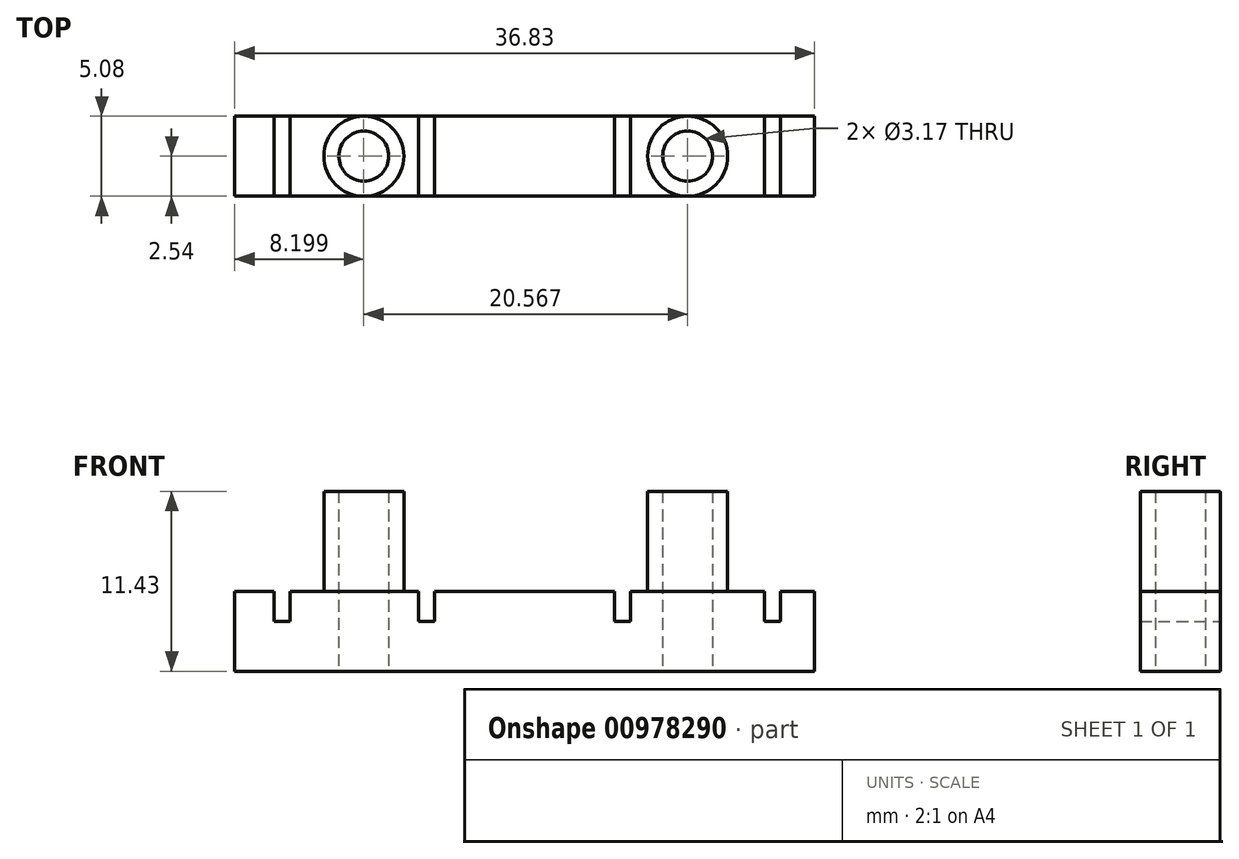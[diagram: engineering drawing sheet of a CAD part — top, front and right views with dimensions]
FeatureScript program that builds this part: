
annotation { "Feature Type Name" : "Feature", "Feature Type Description" : "" }
export const myFeature = defineFeature(function(context is Context, id is Id, definition is map)
    precondition{}
    {
        {
            var Q0;
            Q0=qCreatedBy(makeId("Top.planeOp"),FACE);
            var sketch = newSketch(context, id + "F0", { "sketchPlane" : qUnion([Q0])});
            skLineSegment(sketch, "E0.bottom", {"start": v(-18.67, 0) * mm, "end": v(18.16, 0) * mm});
            skLineSegment(sketch, "E0.top", {"start": v(-18.67, 5.08) * mm, "end": v(18.16, 5.08) * mm});
            skLineSegment(sketch, "E0.left", {"start": v(-18.67, 0) * mm, "end": v(-18.67, 5.08) * mm});
            skLineSegment(sketch, "E0.right", {"start": v(18.16, 0) * mm, "end": v(18.16, 5.08) * mm});
            skSolve(sketch);
        }
        {
            var Q0;
            Q0=makeQuery(id+"F0.imprint","IMPRINT",FACE,{"disambiguationData":[TD([[makeQuery(id+"F0.imprint","IMPRINT",EDGE,{"derivedFrom":sQuery(id+"F0.wireOp",EDGE,"E0.bottom")}),1.0]])]});
            extrude(context, id + "F1", {"entities" : qUnion([Q0]), "depth" : 5.08 * mm, "offsetDistance" : 25.4 * mm});
        }
        {
            var Q0;
            Q0=makeQuery(id+"F1.opExtrude","SWEPT_FACE",FACE,{"disambiguationData":[OSD([sQuery(id+"F0.wireOp",EDGE,"E0.bottom")])]});
            var sketch = newSketch(context, id + "F2", { "sketchPlane" : qUnion([Q0])});
            skCircle(sketch, "E1.cCircle", {"center": v(-15.5, 5.1) * mm, "radius": 0.73 * mm, "construction": true});
            skLineSegment(sketch, "E1.0", {"start": v(-14.22, 5.84) * mm, "end": v(-15.5, 3.64) * mm});
            skLineSegment(sketch, "E1.1", {"start": v(-15.5, 3.64) * mm, "end": v(-16.76, 5.84) * mm});
            skLineSegment(sketch, "E1.2", {"start": v(-16.76, 5.84) * mm, "end": v(-14.22, 5.84) * mm});
            skPoint(sketch, "E1.0.midPoint", {"position": v(-14.86, 4.74) * mm});
            skCircle(sketch, "E2.cCircle", {"center": v(-5.33, 4.85) * mm, "radius": 0.73 * mm, "construction": true});
            skLineSegment(sketch, "E2.0", {"start": v(-4.06, 5.59) * mm, "end": v(-5.33, 3.39) * mm});
            skLineSegment(sketch, "E2.1", {"start": v(-5.33, 3.39) * mm, "end": v(-6.6, 5.59) * mm});
            skLineSegment(sketch, "E2.2", {"start": v(-6.6, 5.59) * mm, "end": v(-4.06, 5.59) * mm});
            skPoint(sketch, "E2.0.midPoint", {"position": v(-4.7, 4.49) * mm});
            skCircle(sketch, "E3.cCircle", {"center": v(14.99, 5.1) * mm, "radius": 0.73 * mm, "construction": true});
            skLineSegment(sketch, "E3.0", {"start": v(16.26, 5.84) * mm, "end": v(14.99, 3.64) * mm});
            skLineSegment(sketch, "E3.1", {"start": v(14.99, 3.64) * mm, "end": v(13.72, 5.84) * mm});
            skLineSegment(sketch, "E3.2", {"start": v(13.72, 5.84) * mm, "end": v(16.26, 5.84) * mm});
            skPoint(sketch, "E3.0.midPoint", {"position": v(15.62, 4.74) * mm});
            skCircle(sketch, "E4.cCircle", {"center": v(4.83, 5.1) * mm, "radius": 0.73 * mm, "construction": true});
            skLineSegment(sketch, "E4.0", {"start": v(6.1, 5.84) * mm, "end": v(4.83, 3.64) * mm});
            skLineSegment(sketch, "E4.1", {"start": v(4.83, 3.64) * mm, "end": v(3.56, 5.84) * mm});
            skLineSegment(sketch, "E4.2", {"start": v(3.56, 5.84) * mm, "end": v(6.1, 5.84) * mm});
            skPoint(sketch, "E4.0.midPoint", {"position": v(5.46, 4.74) * mm});
            skSolve(sketch);
        }
        {
            var Q0;
            {var subQ0=sQuery(id+"F0.wireOp",EDGE,"E0.bottom");var subQ1=sQuery(id+"F0.wireOp",EDGE,"E0.top");Q0=makeQuery(id+"FROfRwlPDn9hxb0_1.boolean.opBoolean","SPLIT",FACE,{"disambiguationData":[TD([makeQuery(id+"FROfRwlPDn9hxb0_1.opExtrude","SWEPT_FACE",FACE,{"disambiguationData":[OSD([sQuery(id+"F2.wireOp",EDGE,"E2.0")])]})])],"derivedFrom":makeQuery(id+"F1.opExtrude","CAP_FACE",FACE,{"disambiguationData":[OSD([subQ0,subQ1,sQuery(id+"F0.wireOp",EDGE,"E0.left"),sQuery(id+"F0.wireOp",EDGE,"E0.right")])],"isStart":false})});}
            var sketch = newSketch(context, id + "F3", { "sketchPlane" : qUnion([Q0])});
            skCircle(sketch, "E5", {"center": v(-0.25, 2.54) * mm, "radius": 2.54 * mm});
            skPoint(sketch, "E5.centerSnap0", {"position": v(-4.43, 2.54) * mm});
            skPoint(sketch, "E5.centerSnap1", {"position": v(-0.25, 0) * mm});
            skCircle(sketch, "E6", {"center": v(-0.25, 2.54) * mm, "radius": 1.59 * mm});
            skCircle(sketch, "E7", {"center": v(-10.47, 2.54) * mm, "radius": 2.54 * mm});
            skCircle(sketch, "E8", {"center": v(-10.47, 2.54) * mm, "radius": 1.59 * mm});
            skCircle(sketch, "E9", {"center": v(10.1, 2.54) * mm, "radius": 2.54 * mm});
            skCircle(sketch, "E10", {"center": v(10.1, 2.54) * mm, "radius": 1.59 * mm});
            skSolve(sketch);
        }
        {
            var Q0;
            Q0=makeQuery(id+"F3.imprint","IMPRINT",FACE,{"disambiguationData":[TD([[makeQuery(id+"F3.imprint","IMPRINT",EDGE,{"derivedFrom":sQuery(id+"F3.wireOp",EDGE,"E7")}),1.0]])]});
            var Q1;
            Q1=makeQuery(id+"F3.imprint","IMPRINT",FACE,{"disambiguationData":[TD([[makeQuery(id+"F3.imprint","IMPRINT",EDGE,{"derivedFrom":sQuery(id+"F3.wireOp",EDGE,"E9")}),1.0]])]});
            extrude(context, id + "F4", {"entities" : qUnion([Q0, Q1]), "operationType" : NewBodyOperationType.ADD, "depth" : 6.35 * mm, "offsetDistance" : 25.4 * mm});
        }
        {
            var Q0;
            {var subQ0=sQuery(id+"F0.wireOp",EDGE,"E0.bottom");var subQ1=sQuery(id+"F0.wireOp",EDGE,"E0.top");Q0=makeQuery(id+"F4.boolean.opBoolean","SPLIT",FACE,{"disambiguationData":[TD([makeQuery(id+"F4.opExtrude","SWEPT_FACE",FACE,{"disambiguationData":[OSD([sQuery(id+"F3.wireOp",EDGE,"E8")])]})])],"derivedFrom":makeQuery(id+"FROfRwlPDn9hxb0_1.boolean.opBoolean","SPLIT",FACE,{"disambiguationData":[TD([makeQuery(id+"FROfRwlPDn9hxb0_1.opExtrude","SWEPT_FACE",FACE,{"disambiguationData":[OSD([sQuery(id+"F2.wireOp",EDGE,"E1.0")])]})])],"derivedFrom":makeQuery(id+"F1.opExtrude","CAP_FACE",FACE,{"disambiguationData":[OSD([subQ0,subQ1,sQuery(id+"F0.wireOp",EDGE,"E0.left"),sQuery(id+"F0.wireOp",EDGE,"E0.right")])],"isStart":false})})});}
            var Q1;
            {var subQ0=sQuery(id+"F0.wireOp",EDGE,"E0.bottom");var subQ1=sQuery(id+"F0.wireOp",EDGE,"E0.top");Q1=makeQuery(id+"F4.boolean.opBoolean","SPLIT",FACE,{"disambiguationData":[TD([makeQuery(id+"F4.opExtrude","SWEPT_FACE",FACE,{"disambiguationData":[OSD([sQuery(id+"F3.wireOp",EDGE,"E10")])]})])],"derivedFrom":makeQuery(id+"FROfRwlPDn9hxb0_1.boolean.opBoolean","SPLIT",FACE,{"disambiguationData":[TD([makeQuery(id+"FROfRwlPDn9hxb0_1.opExtrude","SWEPT_FACE",FACE,{"disambiguationData":[OSD([sQuery(id+"F2.wireOp",EDGE,"E3.1")])]})])],"derivedFrom":makeQuery(id+"F1.opExtrude","CAP_FACE",FACE,{"disambiguationData":[OSD([subQ0,subQ1,sQuery(id+"F0.wireOp",EDGE,"E0.left"),sQuery(id+"F0.wireOp",EDGE,"E0.right")])],"isStart":false})})});}
            extrude(context, id + "F5", {"entities" : qUnion([Q0, Q1]), "operationType" : NewBodyOperationType.REMOVE, "oppositeDirection" : true, "depth" : 25.4 * mm, "offsetDistance" : 25.4 * mm});
        }
        {
            var Q0;
            Q0=makeQuery(id+"F1.opExtrude","SWEPT_FACE",FACE,{"disambiguationData":[OSD([sQuery(id+"F0.wireOp",EDGE,"E0.top")])]});
            var sketch = newSketch(context, id + "F6", { "sketchPlane" : qUnion([Q0])});
            skLineSegment(sketch, "E11.bottom", {"start": v(-16, 3.18) * mm, "end": v(-14.99, 3.18) * mm});
            skLineSegment(sketch, "E11.top", {"start": v(-16, 8.7) * mm, "end": v(-14.99, 8.7) * mm});
            skLineSegment(sketch, "E11.left", {"start": v(-16, 3.18) * mm, "end": v(-16, 8.7) * mm});
            skLineSegment(sketch, "E11.right", {"start": v(-14.99, 3.18) * mm, "end": v(-14.99, 8.7) * mm});
            skLineSegment(sketch, "E12.bottom", {"start": v(-6.48, 3.18) * mm, "end": v(-5.46, 3.18) * mm});
            skLineSegment(sketch, "E12.top", {"start": v(-6.48, 8.63) * mm, "end": v(-5.46, 8.63) * mm});
            skLineSegment(sketch, "E12.left", {"start": v(-6.48, 3.18) * mm, "end": v(-6.48, 8.63) * mm});
            skLineSegment(sketch, "E12.right", {"start": v(-5.46, 3.18) * mm, "end": v(-5.46, 8.63) * mm});
            skLineSegment(sketch, "E13.bottom", {"start": v(5.97, 3.18) * mm, "end": v(6.99, 3.18) * mm});
            skLineSegment(sketch, "E13.top", {"start": v(5.97, 8.2) * mm, "end": v(6.99, 8.2) * mm});
            skLineSegment(sketch, "E13.left", {"start": v(5.97, 3.18) * mm, "end": v(5.97, 8.2) * mm});
            skLineSegment(sketch, "E13.right", {"start": v(6.99, 3.18) * mm, "end": v(6.99, 8.2) * mm});
            skLineSegment(sketch, "E14.bottom", {"start": v(15.16, 3.18) * mm, "end": v(16.17, 3.18) * mm});
            skLineSegment(sketch, "E14.top", {"start": v(15.16, 7.33) * mm, "end": v(16.17, 7.33) * mm});
            skLineSegment(sketch, "E14.left", {"start": v(15.16, 3.18) * mm, "end": v(15.16, 7.33) * mm});
            skLineSegment(sketch, "E14.right", {"start": v(16.17, 3.18) * mm, "end": v(16.17, 7.33) * mm});
            skSolve(sketch);
        }
        {
            var Q0;
            {var subQ0=sQuery(id+"F6.wireOp",EDGE,"E11.bottom");Q0=makeQuery(id+"F6.imprint","IMPRINT",FACE,{"disambiguationData":[TD([[makeQuery(id+"F6.imprint","IMPRINT",EDGE,{"derivedFrom":subQ0}),1.0]])]});}
            var Q1;
            {var subQ0=sQuery(id+"F6.wireOp",EDGE,"E12.bottom");Q1=makeQuery(id+"F6.imprint","IMPRINT",FACE,{"disambiguationData":[TD([[makeQuery(id+"F6.imprint","IMPRINT",EDGE,{"derivedFrom":subQ0}),1.0]])]});}
            var Q2;
            {var subQ0=sQuery(id+"F6.wireOp",EDGE,"E13.bottom");Q2=makeQuery(id+"F6.imprint","IMPRINT",FACE,{"disambiguationData":[TD([[makeQuery(id+"F6.imprint","IMPRINT",EDGE,{"derivedFrom":subQ0}),1.0]])]});}
            var Q3;
            {var subQ0=sQuery(id+"F6.wireOp",EDGE,"E14.bottom");Q3=makeQuery(id+"F6.imprint","IMPRINT",FACE,{"disambiguationData":[TD([[makeQuery(id+"F6.imprint","IMPRINT",EDGE,{"derivedFrom":subQ0}),1.0]])]});}
            extrude(context, id + "F7", {"entities" : qUnion([Q0, Q1, Q2, Q3]), "operationType" : NewBodyOperationType.REMOVE, "oppositeDirection" : true, "depth" : 25.4 * mm, "offsetDistance" : 25.4 * mm});
        }
    });
